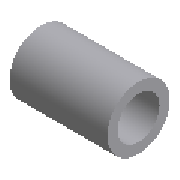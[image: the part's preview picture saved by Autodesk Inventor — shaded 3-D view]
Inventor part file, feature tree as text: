
AUTODESK INVENTOR PART (.ipt)
format: ipt  version: 2023 (Build 270158000, 158)  size: 156,160 bytes
history: native  units: mm (DEFAULTED — no unit token found)
features: other x6, revolve x1, sketch x1
ambient origin geometry x8: Origin, YZ Plane, XZ Plane, XY Plane, X Axis, Y Axis, Z Axis, Center Point
bodies: Solid1 (feature_tree)
feature tree (8):
  revolve  "Revolution1"  [1 undecoded]
  other  "Work Point1"
  other  "Work Point2"
  other  "Work Axis1"
  other  "Work Point3"
  other  "Work Axis2"
  other  "Work Point4"
  sketch  "Sketch1"  dims[d0=49.1mm d1=41.2mm d2=60.3mm d10=90.0deg d4=12.7mm d5=12.7mm]
note: 1 required parameter value undecoded (feature->parameter linkage not recoverable at this tier; creation-order binding heuristic only, values carry confidence <= 0.55)
